# Revit family: Sink-Undermount-Acorn-DUADA-3118-55_Series
name_source: partatom
category: Plumbing Fixtures
units: mm (PartAtom-declared; Revit-internal decimal feet)

## family parameters
Cut with Voids When Loaded = No
Host = Face
OmniClass Number = 23.45.05.14.14
OmniClass Title = Sinks/Lavatories
Part Type = Normal
Room Calculation Point = No
Round Connector Dimension = Use Diameter
Shared = Yes

## types (1)
- DUADA-3118-55
    ADA Compliant = Yes
    Assembly Code = D2010440
    Bowl Length = 16"
    Bowl Width = 13 1/2"
    CW Connection = No
    CWFU = 3
    Compliance Certifications = ASME A112.19.3/CSA B45.4, IAPMO® Certified
    Default Elevation = 34"
    Description = Stainless Steel Undermount Sink
    Drain Opening Size = 3 1/2"
    Finish = Stainless Steel-Acorn-Satin
    HW Connection = No
    HWFU = 3
    Height = 5 1/2"
    Installation Type = Wall Mounted
    Length = 18 1/2"
    Manufacturer = Acorn
    Material = Stainless Steel-Acorn-Satin
    Model = DUADA-3118-55
    URL = https://www.acorneng.com
    Vent Connection = No
    WFU = 4
    Waste Connection = No
    Width = 30 3/4"

## geometry (parser evidence)
native form markers: Sweep x3
no freeform markers — native parametric forms only
